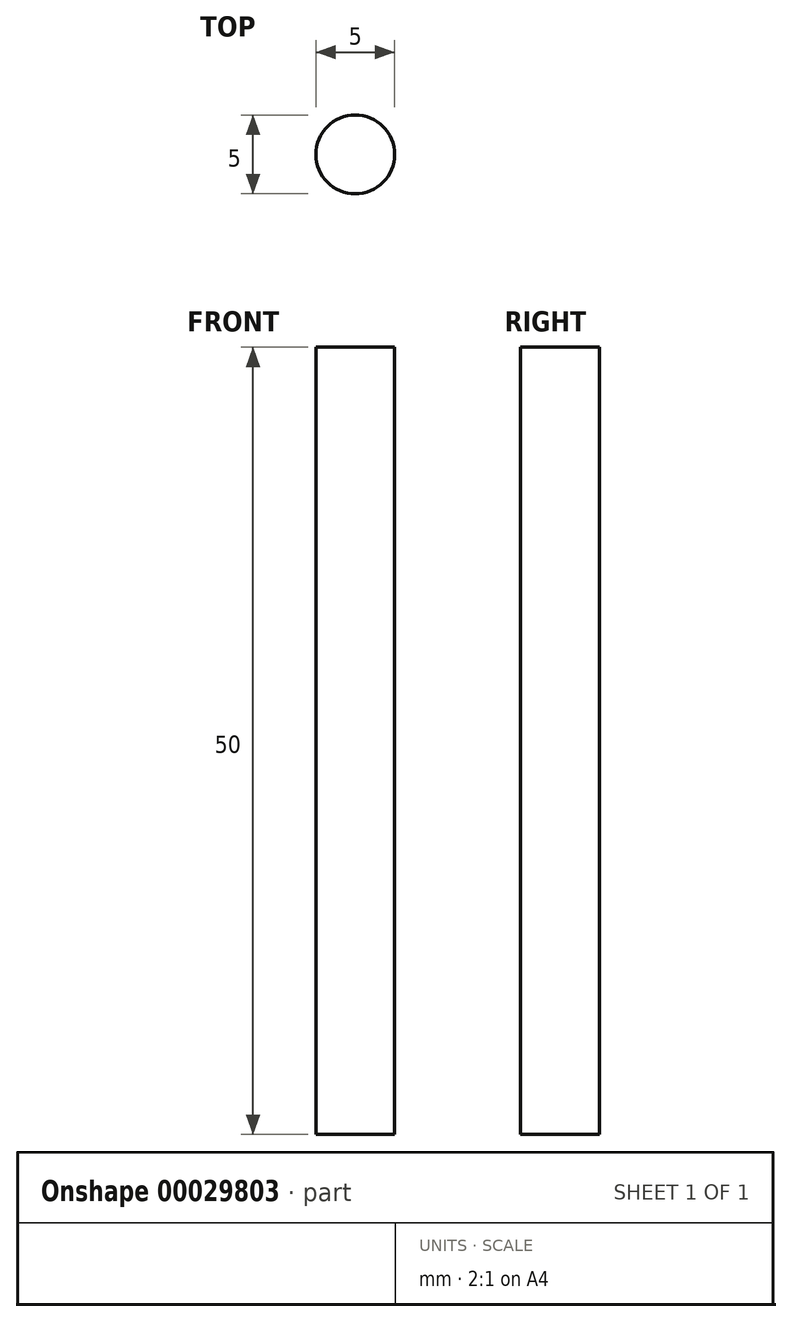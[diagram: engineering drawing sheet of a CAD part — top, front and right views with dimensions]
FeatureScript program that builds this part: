
annotation { "Feature Type Name" : "Feature", "Feature Type Description" : "" }
export const myFeature = defineFeature(function(context is Context, id is Id, definition is map)
    precondition{}
    {
        {
            var Q0;
            Q0=qCreatedBy(makeId("Top.planeOp"),FACE);
            var sketch = newSketch(context, id + "F0", { "sketchPlane" : qUnion([Q0])});
            skCircle(sketch, "E0", {"center": v(0, 0) * mm, "radius": 2.5 * mm});
            skSolve(sketch);
        }
        {
            var Q0;
            Q0 = qSketchRegion(id + "F0", true);
            extrude(context, id + "F1", {"entities" : qUnion([Q0]), "depth" : 50 * mm});
        }
    });
